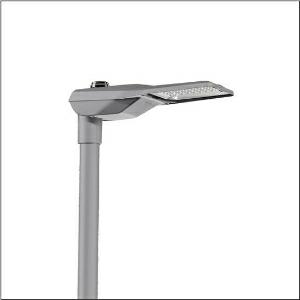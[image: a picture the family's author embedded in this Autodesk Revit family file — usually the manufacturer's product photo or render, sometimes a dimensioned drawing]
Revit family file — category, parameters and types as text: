
# Revit family: streetlight_sl_21_mini___st1_0a_5xe6d67n08jb_11ba
name_source: partatom
category: Lighting Fixtures
units: mm (PartAtom-declared; Revit-internal decimal feet)

## family parameters
Cut with Voids When Loaded = No
Host = Face
Light Source = No
Part Type = Normal
Room Calculation Point = No
Round Connector Dimension = Use Diameter
Shared = No

## types (1)
- --- (1 x LED, 11500 lm, 87.3 W, 2700K)
    Apparent Load = 87 VA
    CIE Flux Codes = 40 73 97 100 100
    Color Rendering = 70
    Color Temperature = 2700K
    Default Elevation = 1800 mm
    Description = Streetlight SL 21 mini, mast luminaire, primary light control with lens, of PMMA, primary optical cover: cover, of toughened safety glass, transparent, light distribution: ST1.0a, light emission: direct distribution, primary light characteristic: asymmetric, installation type: side-entry, LED, 3G 2.5mm², High Power LED, rated luminous flux: 11.500lm, luminous efficacy: 132lm/W, light colour: 727, colour temperature: 2700K, control gear: NEMA (7pin), control: overheat protection, pre-setting: linear dimming characteristic, constant luminous flux control, time-dependent luminous flux control, flexible luminous flux parameterisation, mains connection: 230..240V, AC, 50/60Hz, connection cable pre-assembled, cable length: 10,5m, wiring characteristics: H05VV-F, start of lifetime: 87W, end of service life: 90W, reduction: 40W, luminaire housing, of diecast aluminium (EN AC-44300), powder-coated, SITECO metallic grey (DB 702S), corrosivity category C5 high according to DIN EN ISO 12944, multi-level sealing system, sealing non-destructively replaceable, inclination adjustable: 0°, 5°, 10°, 15°, length: 628mm, width: 235mm, height: 110mm, spigot size: 42mm (side-entry), mounting height: 4..8m, protection rating (complete): IP66, insulation class (complete): insulation class I (protective earthing), certification: CE, ENEC, ENEC+, VDE, impact resistance: IK10, permissible operating ambient temperature for outdoor applications: -40..+50°C, standard-compliant lighting for roads and squares, packaging unit: 1 piece

Light Distribution: ST1.0a
    Height = 110 mm
    Lamp = 1 x LED
    Lamp Light Flux = 11500 lm
    Lamp Power = 87.3 W
    Lamp count = 1
    Length = 625 mm
    Luminous efficacy = 132 lm/W
    Manufacturer = Siteco
    ModVariant = No
    Model = 5XE6D67N08JB
    Number of Poles = 1
    OnlyDefault = Yes
    Power Factor = 1
    Product Name = Streetlight SL 21 mini | ST1.0a
    Product group = mast luminaire | pylon top
    ProductGroupID = 6100
    Protection Class = Protection class I
    Protection Degree = IP 66
    RLX_Detail_Level = 1
    RLX_Emergency_Light_Flux = 0 lm
    RLX_Emergency_Type = 0
    RLX_Emergency_Type_DB = No
    RlxData = <blob elided: 26093 chars, md5=a2054618>
    Socket = socket
    Standby Power = 0 W
    System Light Flux = 11500 lm
    System Power = 87 W
    Type Comments = factory setting: luminous flux: 100 % | dim-lin: 254 | 915 mA
    Type Image = l_1294379.jpg
    URL = http://relux.com
    VarID = @adj_134737
    Voltage = 0 V
    Weight = 0.00 kg
    Width = 234 mm

## geometry (parser evidence)
native form markers: Blend x4, Sweep x10
no freeform markers — native parametric forms only
